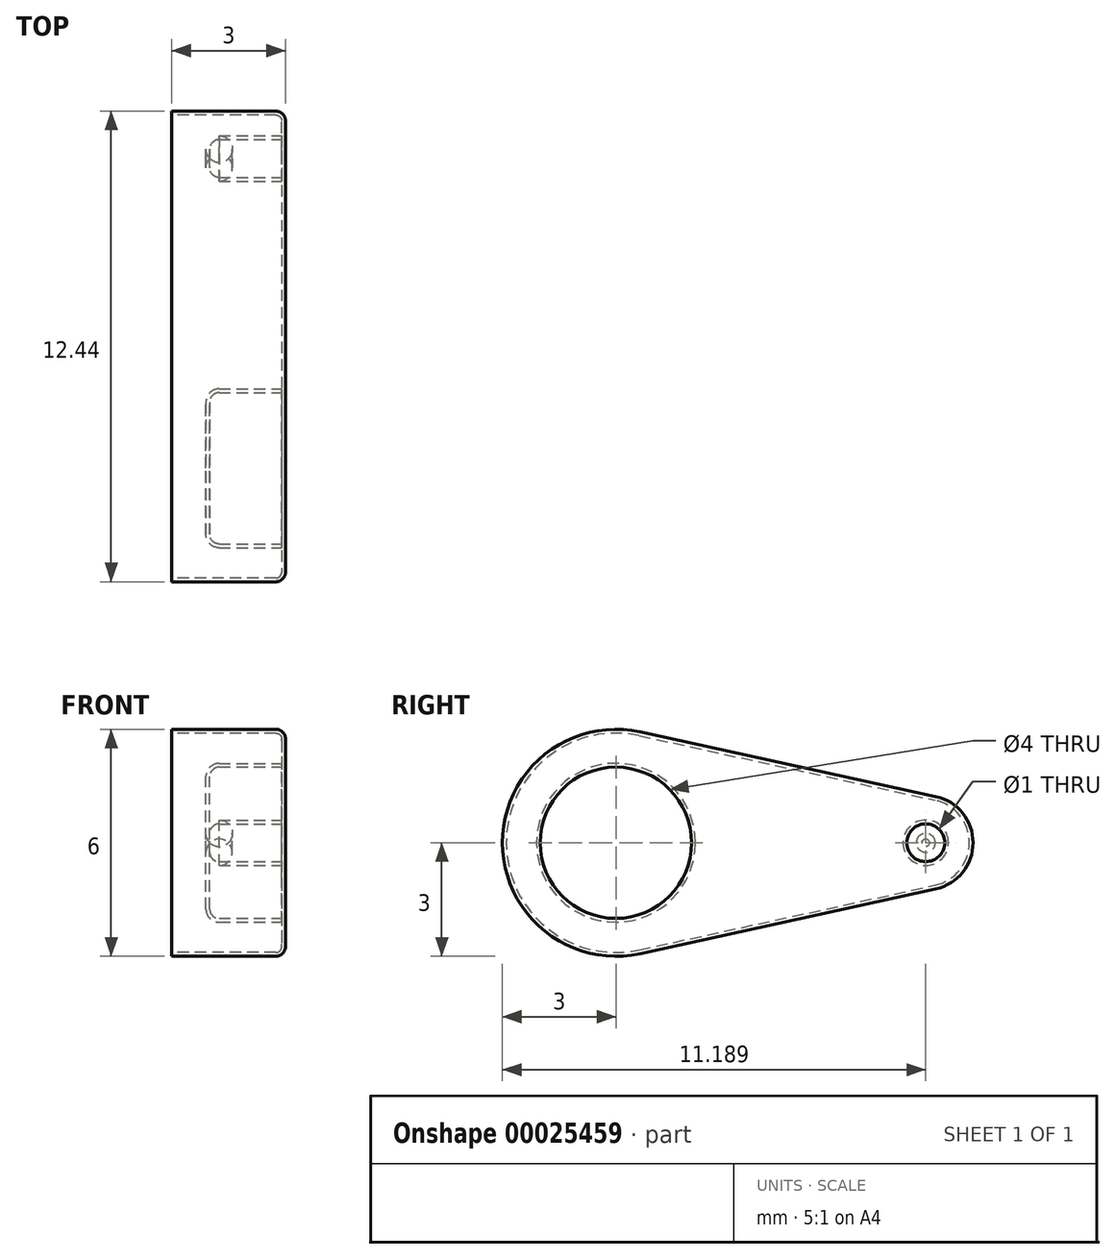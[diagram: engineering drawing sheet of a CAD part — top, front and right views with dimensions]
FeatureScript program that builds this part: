
annotation { "Feature Type Name" : "Feature", "Feature Type Description" : "" }
export const myFeature = defineFeature(function(context is Context, id is Id, definition is map)
    precondition{}
    {
        {
            var Q0;
            Q0=qCreatedBy(makeId("Right.planeOp"),FACE);
            var sketch = newSketch(context, id + "F0", { "sketchPlane" : qUnion([Q0])});
            skCircle(sketch, "E0", {"center": v(0, 0) * mm, "radius": 3 * mm});
            skCircle(sketch, "E1", {"center": v(8.19, 0) * mm, "radius": 1.25 * mm});
            skLineSegment(sketch, "E2", {"start": v(0.64, 2.93) * mm, "end": v(8.46, 1.22) * mm});
            skLineSegment(sketch, "E3", {"start": v(0.64, -2.93) * mm, "end": v(8.46, -1.22) * mm});
            skSolve(sketch);
        }
        {
            var Q0;
            {var subQ0=sQuery(id+"F0.wireOp",EDGE,"E0");var subQ2=makeQuery(id+"F0.imprint","INTERSECT",VERTEX,{"derivedFrom":[subQ0,sQuery(id+"F0.wireOp",EDGE,"E2")]});Q0=makeQuery(id+"F0.imprint","IMPRINT",FACE,{"disambiguationData":[TD([[makeQuery(id+"F0.imprint","IMPRINT",EDGE,{"disambiguationData":[TD([[subQ2,-1.0]])],"derivedFrom":subQ0}),1.0]])]});}
            var Q1;
            {var subQ0=sQuery(id+"F0.wireOp",EDGE,"E1");var subQ2=makeQuery(id+"F0.imprint","INTERSECT",VERTEX,{"derivedFrom":[subQ0,sQuery(id+"F0.wireOp",EDGE,"E2")]});Q1=makeQuery(id+"F0.imprint","IMPRINT",FACE,{"disambiguationData":[TD([[makeQuery(id+"F0.imprint","IMPRINT",EDGE,{"disambiguationData":[TD([[subQ2,-1.0]])],"derivedFrom":subQ0}),1.0]])]});}
            var Q2;
            {var subQ1=sQuery(id+"F0.wireOp",EDGE,"E2");Q2=makeQuery(id+"F0.imprint","IMPRINT",FACE,{"disambiguationData":[TD([[makeQuery(id+"F0.imprint","IMPRINT",EDGE,{"derivedFrom":subQ1}),-1.0]])]});}
            extrude(context, id + "F1", {"entities" : qUnion([Q0, Q1, Q2]), "depth" : 3 * mm});
        }
        {
            var Q0;
            Q0=makeQuery(id+"F1.opExtrude","CAP_FACE",FACE,{"disambiguationData":[OSD([sQuery(id+"F0.wireOp",EDGE,"E0"),sQuery(id+"F0.wireOp",EDGE,"E1"),sQuery(id+"F0.wireOp",EDGE,"E2"),sQuery(id+"F0.wireOp",EDGE,"E3")])],"isStart":false});
            var sketch = newSketch(context, id + "F2", { "sketchPlane" : qUnion([Q0])});
            skCircle(sketch, "E4", {"center": v(0, 0) * mm, "radius": 2 * mm});
            skCircle(sketch, "E5", {"center": v(8.19, 0) * mm, "radius": 0.5 * mm});
            skSolve(sketch);
        }
        {
            var Q0;
            Q0=makeQuery(id+"F2.imprint","IMPRINT",FACE,{"disambiguationData":[TD([[makeQuery(id+"F2.imprint","IMPRINT",EDGE,{"derivedFrom":sQuery(id+"F2.wireOp",EDGE,"E5")}),1.0]])]});
            var Q1;
            Q1=makeQuery(id+"F2.imprint","IMPRINT",FACE,{"disambiguationData":[TD([[makeQuery(id+"F2.imprint","IMPRINT",EDGE,{"derivedFrom":sQuery(id+"F2.wireOp",EDGE,"E4")}),1.0]])]});
            extrude(context, id + "F3", {"entities" : qUnion([Q0, Q1]), "operationType" : NewBodyOperationType.REMOVE, "oppositeDirection" : true, "depth" : 2 * mm});
        }
        {
            var Q0;
            Q0=makeQuery(id+"F3.boolean.opBoolean","COPY",EDGE,{"derivedFrom":makeQuery(id+"F3.opExtrude","CAP_EDGE",EDGE,{"disambiguationData":[OSD([sQuery(id+"F2.wireOp",EDGE,"E4")])],"isStart":true})});
            var Q1;
            Q1=makeQuery(id+"F1.opExtrude","CAP_EDGE",EDGE,{"disambiguationData":[OSD([sQuery(id+"F0.wireOp",EDGE,"E0")])],"isStart":false});
            var Q2;
            Q2=makeQuery(id+"F3.boolean.opBoolean","COPY",EDGE,{"derivedFrom":makeQuery(id+"F3.opExtrude","CAP_EDGE",EDGE,{"disambiguationData":[OSD([sQuery(id+"F2.wireOp",EDGE,"E5")])],"isStart":true})});
            var Q3;
            Q3=makeQuery(id+"F3.boolean.opBoolean","COPY",EDGE,{"derivedFrom":makeQuery(id+"F3.opExtrude","CAP_EDGE",EDGE,{"disambiguationData":[OSD([sQuery(id+"F2.wireOp",EDGE,"E4")])],"isStart":false})});
            var Q4;
            Q4=makeQuery(id+"F3.boolean.opBoolean","COPY",EDGE,{"derivedFrom":makeQuery(id+"F3.opExtrude","CAP_EDGE",EDGE,{"disambiguationData":[OSD([sQuery(id+"F2.wireOp",EDGE,"E5")])],"isStart":false})});
            fillet(context, id + "F4", {"entities" : qUnion([Q0, Q1, Q2, Q3, Q4]), "radius" : .25 * mm, "tangentPropagation" : true, "allowEdgeOverflow" : false});
        }
        {
            var Q0;
            Q0=makeQuery(id+"F1.opExtrude","CAP_FACE",FACE,{"disambiguationData":[OSD([sQuery(id+"F0.wireOp",EDGE,"E0"),sQuery(id+"F0.wireOp",EDGE,"E1"),sQuery(id+"F0.wireOp",EDGE,"E2"),sQuery(id+"F0.wireOp",EDGE,"E3")])],"isStart":true});
            shell(context, id + "F5", {"entities" : qUnion([Q0]), "thickness" : .1 * mm});
        }
    });
